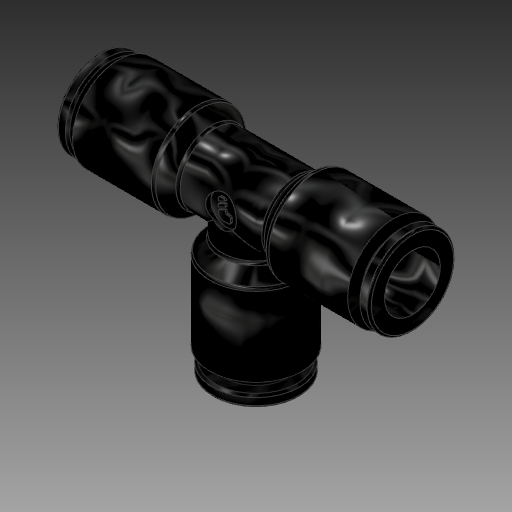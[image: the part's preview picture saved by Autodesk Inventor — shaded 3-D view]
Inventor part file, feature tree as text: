
AUTODESK INVENTOR PART (.ipt)
format: ipt  version: 2017.1 (Build 211199000, 199)  size: 324,608 bytes
history: native  units: in
note: dims shown in document units (in); Inventor stores cm internally (conversion verified against a paired STEP export)
features: extrude x2, sketch x2
ambient origin geometry x8: Origin, YZ Plane, XZ Plane, XY Plane, X Axis, Y Axis, Z Axis, Center Point
bodies: Solid1 (feature_tree)
feature tree (4):
  extrude  "Extrusion1"  Depth=1.0in TaperAngle=0.0deg
  extrude  "Extrusion2"  Depth=0.578in TaperAngle=0.0deg
  sketch  "Sketch1"  dims[d0=0.25in d1=1.0in d2=0.0in]
  sketch  "Sketch2"  dims[d3=0.25in d4=0.578in d5=0.0in]
